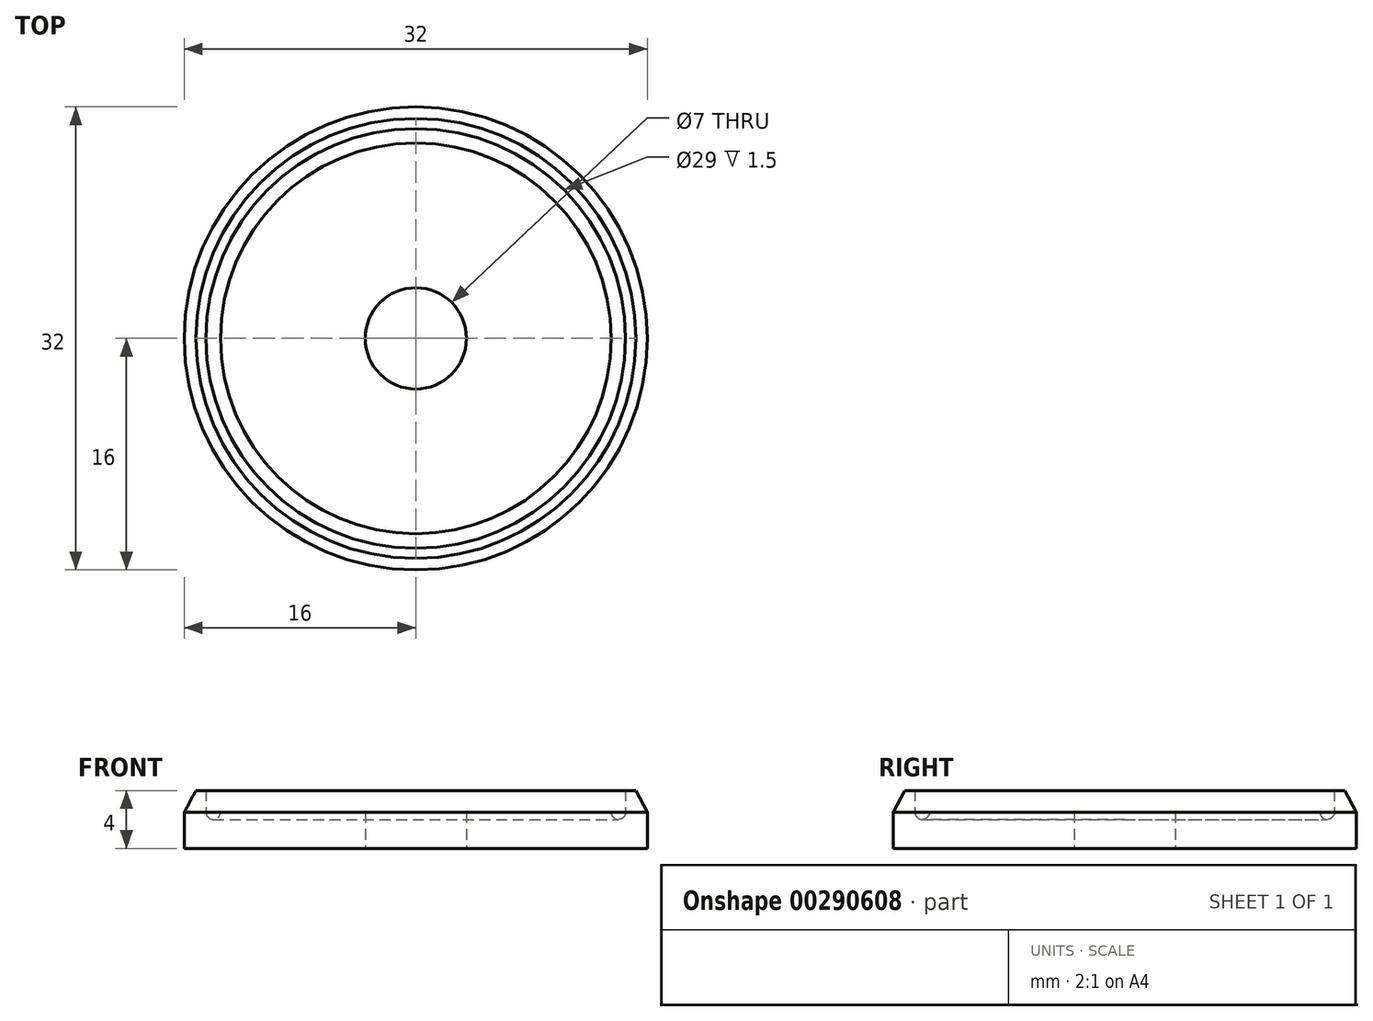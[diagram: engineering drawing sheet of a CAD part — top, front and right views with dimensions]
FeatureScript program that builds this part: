
annotation { "Feature Type Name" : "Feature", "Feature Type Description" : "" }
export const myFeature = defineFeature(function(context is Context, id is Id, definition is map)
    precondition{}
    {
        {
            var Q0;
            Q0=qCreatedBy(makeId("Front.planeOp"),FACE);
            var sketch = newSketch(context, id + "F0", { "sketchPlane" : qUnion([Q0])});
            skLineSegment(sketch, "E0", {"start": v(0, 0) * mm, "end": v(0, 4) * mm, "construction": true});
            skLineSegment(sketch, "E1", {"start": v(3.5, 0) * mm, "end": v(16, 0) * mm});
            skLineSegment(sketch, "E2", {"start": v(16, 0) * mm, "end": v(16, 2.5) * mm});
            skLineSegment(sketch, "E3", {"start": v(16, 2.5) * mm, "end": v(15.2, 4) * mm});
            skLineSegment(sketch, "E4", {"start": v(15.2, 4) * mm, "end": v(14.5, 4) * mm});
            skLineSegment(sketch, "E5", {"start": v(14.5, 4) * mm, "end": v(14.5, 2.5) * mm});
            skLineSegment(sketch, "E6", {"start": v(14, 2) * mm, "end": v(14, 2) * mm});
            skLineSegment(sketch, "E7", {"start": v(13.5, 2.5) * mm, "end": v(13.5, 2.5) * mm});
            skLineSegment(sketch, "E8", {"start": v(13.5, 2.5) * mm, "end": v(3.5, 2.5) * mm});
            skLineSegment(sketch, "E9", {"start": v(3.5, 2.5) * mm, "end": v(3.5, 0) * mm});
            skPoint(sketch, "E10.visualSharp", {"position": v(13.5, 2) * mm});
            skArc(sketch, "E10.filletArc", {"start": v(13.5, 2.5) * mm, "mid": v(13.54, 2.3) * mm, "end": v(13.65, 2.15) * mm});
            skPoint(sketch, "E11.visualSharp", {"position": v(14, 2) * mm});
            skArc(sketch, "E11.filletArc", {"start": v(13.65, 2.15) * mm, "mid": v(13.8, 2.04) * mm, "end": v(14, 2) * mm});
            skPoint(sketch, "E12.visualSharp", {"position": v(14.5, 2) * mm});
            skArc(sketch, "E12.filletArc", {"start": v(14, 2) * mm, "mid": v(14.35, 2.15) * mm, "end": v(14.5, 2.5) * mm});
            skSolve(sketch);
        }
        {
            var Q0;
            Q0=makeQuery(id+"F0.imprint","IMPRINT",FACE,{"disambiguationData":[TD([[makeQuery(id+"F0.imprint","IMPRINT",EDGE,{"derivedFrom":sQuery(id+"F0.wireOp",EDGE,"E1")}),1.0]])]});
            var Q1;
            Q1=sQuery(id+"F0.wireOp",EDGE,"E0");
            revolve(context, id + "F1", {"entities" : qUnion([Q0]), "axis" : qUnion([Q1]), "revolveType" : RevolveType.FULL});
        }
    });
